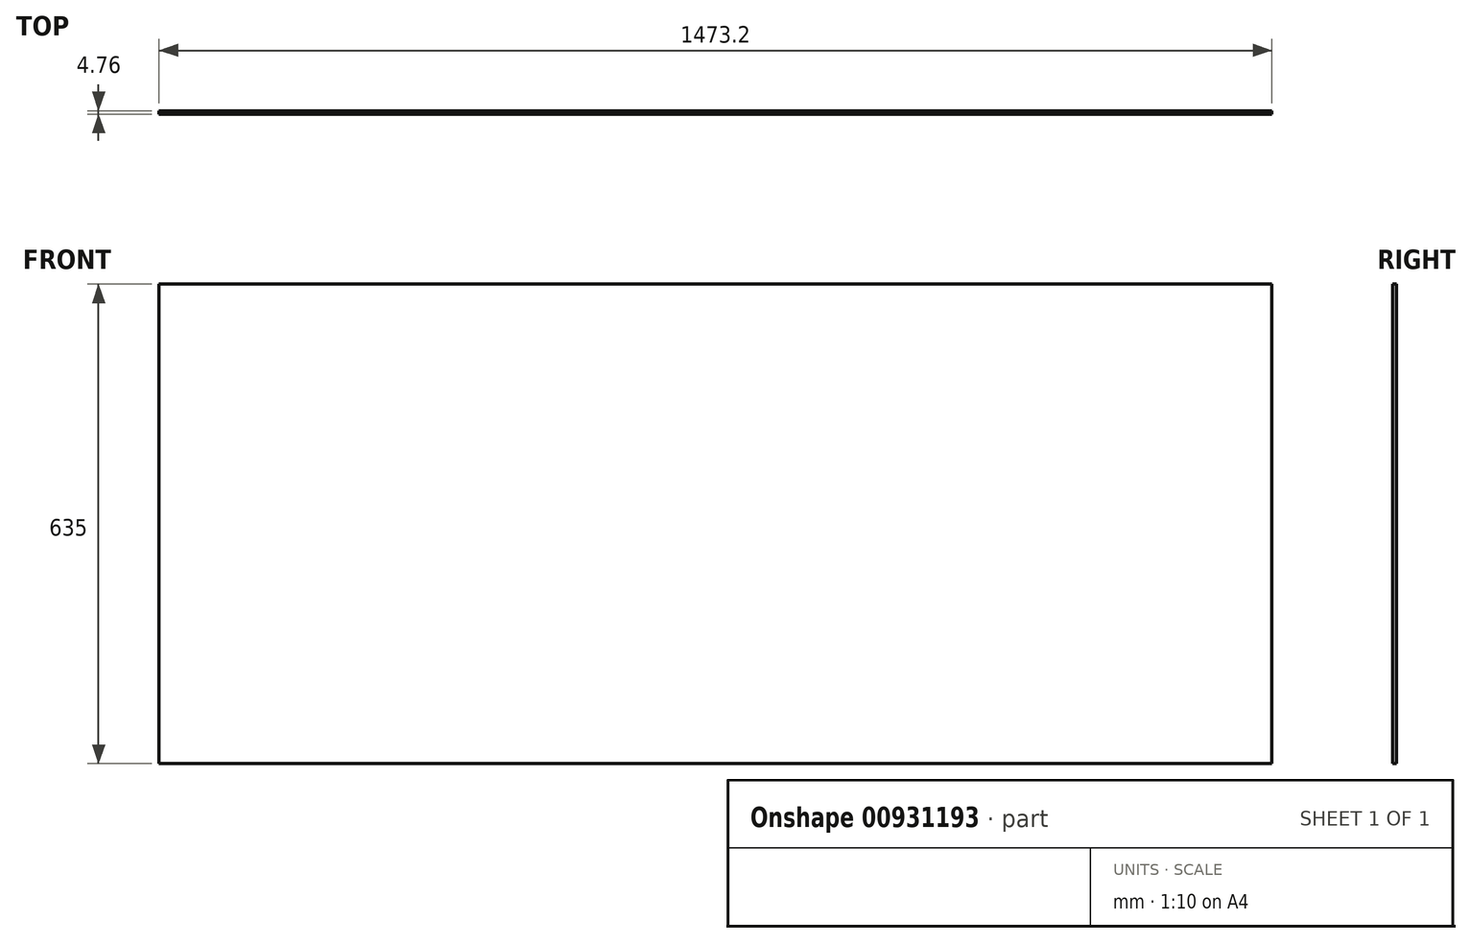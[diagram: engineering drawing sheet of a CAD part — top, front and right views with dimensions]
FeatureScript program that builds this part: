
annotation { "Feature Type Name" : "Feature", "Feature Type Description" : "" }
export const myFeature = defineFeature(function(context is Context, id is Id, definition is map)
    precondition{}
    {
        {
            var Q0;
            Q0=qCreatedBy(makeId("Front.planeOp"),FACE);
            var sketch = newSketch(context, id + "F0", { "sketchPlane" : qUnion([Q0])});
            skLineSegment(sketch, "E0.bottom", {"start": v(0, 0) * mm, "end": v(1473.2, 0) * mm});
            skLineSegment(sketch, "E0.top", {"start": v(0, 635) * mm, "end": v(1473.2, 635) * mm});
            skLineSegment(sketch, "E0.left", {"start": v(0, 0) * mm, "end": v(0, 635) * mm});
            skLineSegment(sketch, "E0.right", {"start": v(1473.2, 0) * mm, "end": v(1473.2, 635) * mm});
            skSolve(sketch);
        }
        {
            var Q0;
            Q0=makeQuery(id+"F0.imprint","IMPRINT",FACE,{"disambiguationData":[TD([[makeQuery(id+"F0.imprint","IMPRINT",EDGE,{"derivedFrom":sQuery(id+"F0.wireOp",EDGE,"E0.bottom")}),1.0]])]});
            extrude(context, id + "F1", {"entities" : qUnion([Q0]), "oppositeDirection" : true, "depth" : 4.76 * mm, "offsetDistance" : 25.4 * mm});
        }
    });
